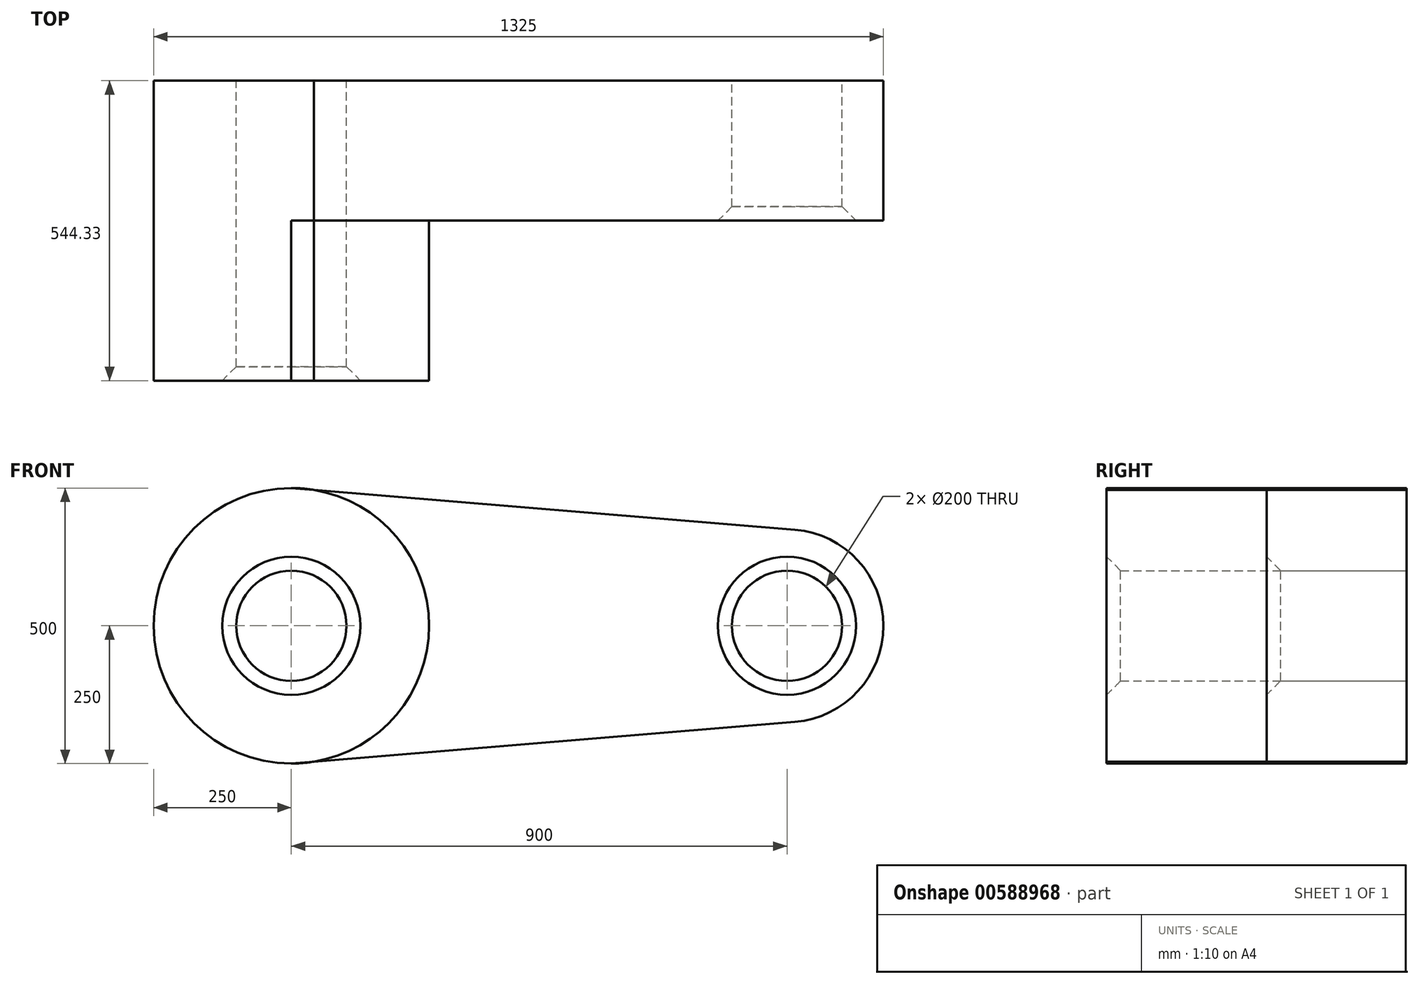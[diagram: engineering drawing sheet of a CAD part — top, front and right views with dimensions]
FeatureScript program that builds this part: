
annotation { "Feature Type Name" : "Feature", "Feature Type Description" : "" }
export const myFeature = defineFeature(function(context is Context, id is Id, definition is map)
    precondition{}
    {
        {
            var Q0;
            Q0=qCreatedBy(makeId("Front.planeOp"),FACE);
            var sketch = newSketch(context, id + "F0", { "sketchPlane" : qUnion([Q0])});
            skCircle(sketch, "E0", {"center": v(0, 0) * mm, "radius": 250 * mm});
            skCircle(sketch, "E1", {"center": v(900, 0) * mm, "radius": 175 * mm});
            skLineSegment(sketch, "E2", {"start": v(0, 250) * mm, "end": v(914.42, 174.4) * mm});
            skLineSegment(sketch, "E3", {"start": v(0, -250) * mm, "end": v(914.42, -174.4) * mm});
            skCircle(sketch, "E4", {"center": v(0, 0) * mm, "radius": 100 * mm});
            skCircle(sketch, "E5", {"center": v(900, 0) * mm, "radius": 100 * mm});
            skSolve(sketch);
        }
        {
            var Q0;
            Q0 = qSketchRegion(id + "F0", true);
            extrude(context, id + "F1", {"entities" : qUnion([Q0]), "depth" : 254 * mm, "offsetDistance" : 25.4 * mm});
        }
        {
            var Q0;
            Q0=makeQuery(id+"F0.imprint","IMPRINT",FACE,{"disambiguationData":[TD([[makeQuery(id+"F0.imprint","IMPRINT",EDGE,{"derivedFrom":sQuery(id+"F0.wireOp",EDGE,"E4")}),-1.0]])]});
            extrude(context, id + "F2", {"entities" : qUnion([Q0]), "operationType" : NewBodyOperationType.ADD, "depth" : 544.33 * mm, "offsetDistance" : 25.4 * mm});
        }
        {
            var Q0;
            {var subQ0=sQuery(id+"F0.wireOp",EDGE,"E0");Q0=makeQuery(id+"F2.opExtrude","CAP_EDGE",EDGE,{"disambiguationData":[OSD([subQ0]),TDD([makeQuery(id+"F0.imprint","IMPRINT",EDGE,{"disambiguationData":[TD([[makeQuery(id+"F0.imprint","INTERSECT",VERTEX,{"disambiguationData":[OD(1.0)],"derivedFrom":[subQ0,sQuery(id+"F0.wireOp",EDGE,"E2")]}),1.0]])],"derivedFrom":subQ0})])],"isStart":false});}
            var Q1;
            Q1=makeQuery(id+"F2.opExtrude","CAP_EDGE",EDGE,{"disambiguationData":[OSD([sQuery(id+"F0.wireOp",EDGE,"E4")])],"isStart":false});
            var Q2;
            Q2=makeQuery(id+"F1.opExtrude","CAP_EDGE",EDGE,{"disambiguationData":[OSD([sQuery(id+"F0.wireOp",EDGE,"E5")])],"isStart":false});
            var Q3;
            {var subQ0=sQuery(id+"F0.wireOp",EDGE,"E2");var subQ1=sQuery(id+"F0.wireOp",EDGE,"E0");var subQ2=sQuery(id+"F0.wireOp",EDGE,"E3");Q3=makeQuery(id+"F2.boolean.opBoolean","INTERSECT",EDGE,{"derivedFrom":[makeQuery(id+"F1.opExtrude","CAP_FACE",FACE,{"disambiguationData":[OSD([subQ1,sQuery(id+"F0.wireOp",EDGE,"E1"),subQ0,subQ2,sQuery(id+"F0.wireOp",EDGE,"E4"),sQuery(id+"F0.wireOp",EDGE,"E5")])],"isStart":false}),makeQuery(id+"F2.opExtrude","SWEPT_FACE",FACE,{"disambiguationData":[OSD([subQ1]),TDD([makeQuery(id+"F0.imprint","IMPRINT",EDGE,{"disambiguationData":[TD([[makeQuery(id+"F0.imprint","INTERSECT",VERTEX,{"disambiguationData":[OD(1.0)],"derivedFrom":[subQ1,subQ0]}),1.0]])],"derivedFrom":subQ1})])]})]});}
            chamfer(context, id + "F3", {"entities" : qUnion([Q0, Q1, Q2, Q3]), "chamferType" : ChamferType.TWO_OFFSETS, "width1" : 25.4 * mm, "oppositeDirection" : false, "width2" : 25.4 * mm, "tangentPropagation" : true});
        }
    });
